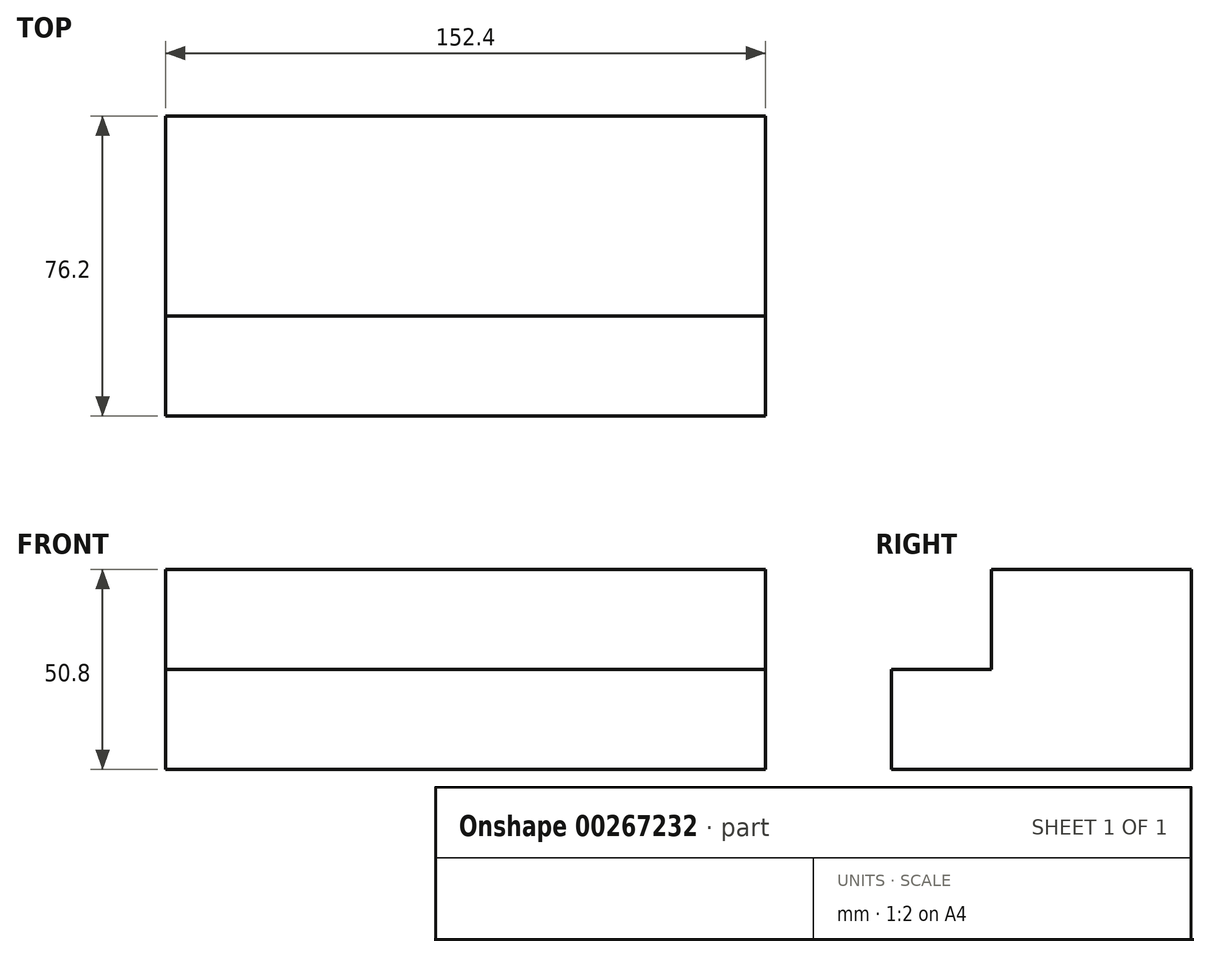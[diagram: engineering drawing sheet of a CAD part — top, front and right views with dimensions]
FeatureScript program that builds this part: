
annotation { "Feature Type Name" : "Feature", "Feature Type Description" : "" }
export const myFeature = defineFeature(function(context is Context, id is Id, definition is map)
    precondition{}
    {
        {
            var Q0;
            Q0=qCreatedBy(makeId("Right.planeOp"),FACE);
            var sketch = newSketch(context, id + "F0", { "sketchPlane" : qUnion([Q0])});
            skLineSegment(sketch, "E0.bottom", {"start": v(-25.7, 0) * mm, "end": v(25.1, 0) * mm});
            skLineSegment(sketch, "E0.top", {"start": v(-51.1, -50.8) * mm, "end": v(25.1, -50.8) * mm});
            skLineSegment(sketch, "E0.left", {"start": v(-51.1, -25.4) * mm, "end": v(-51.1, -50.8) * mm});
            skLineSegment(sketch, "E0.right", {"start": v(25.1, 0) * mm, "end": v(25.1, -50.8) * mm});
            skLineSegment(sketch, "E1.top", {"start": v(-51.1, -25.4) * mm, "end": v(-25.7, -25.4) * mm});
            skLineSegment(sketch, "E1.right", {"start": v(-25.7, 0) * mm, "end": v(-25.7, -25.4) * mm});
            skPoint(sketch, "E2.orphan", {"position": v(-51.1, 0) * mm});
            skSolve(sketch);
        }
        {
            var Q0;
            Q0=makeQuery(id+"F0.imprint","IMPRINT",FACE,{"disambiguationData":[TD([[makeQuery(id+"F0.imprint","IMPRINT",EDGE,{"derivedFrom":sQuery(id+"F0.wireOp",EDGE,"E0.bottom")}),-1.0]])]});
            extrude(context, id + "F1", {"entities" : qUnion([Q0]), "depth" : 152.4 * mm});
        }
    });
